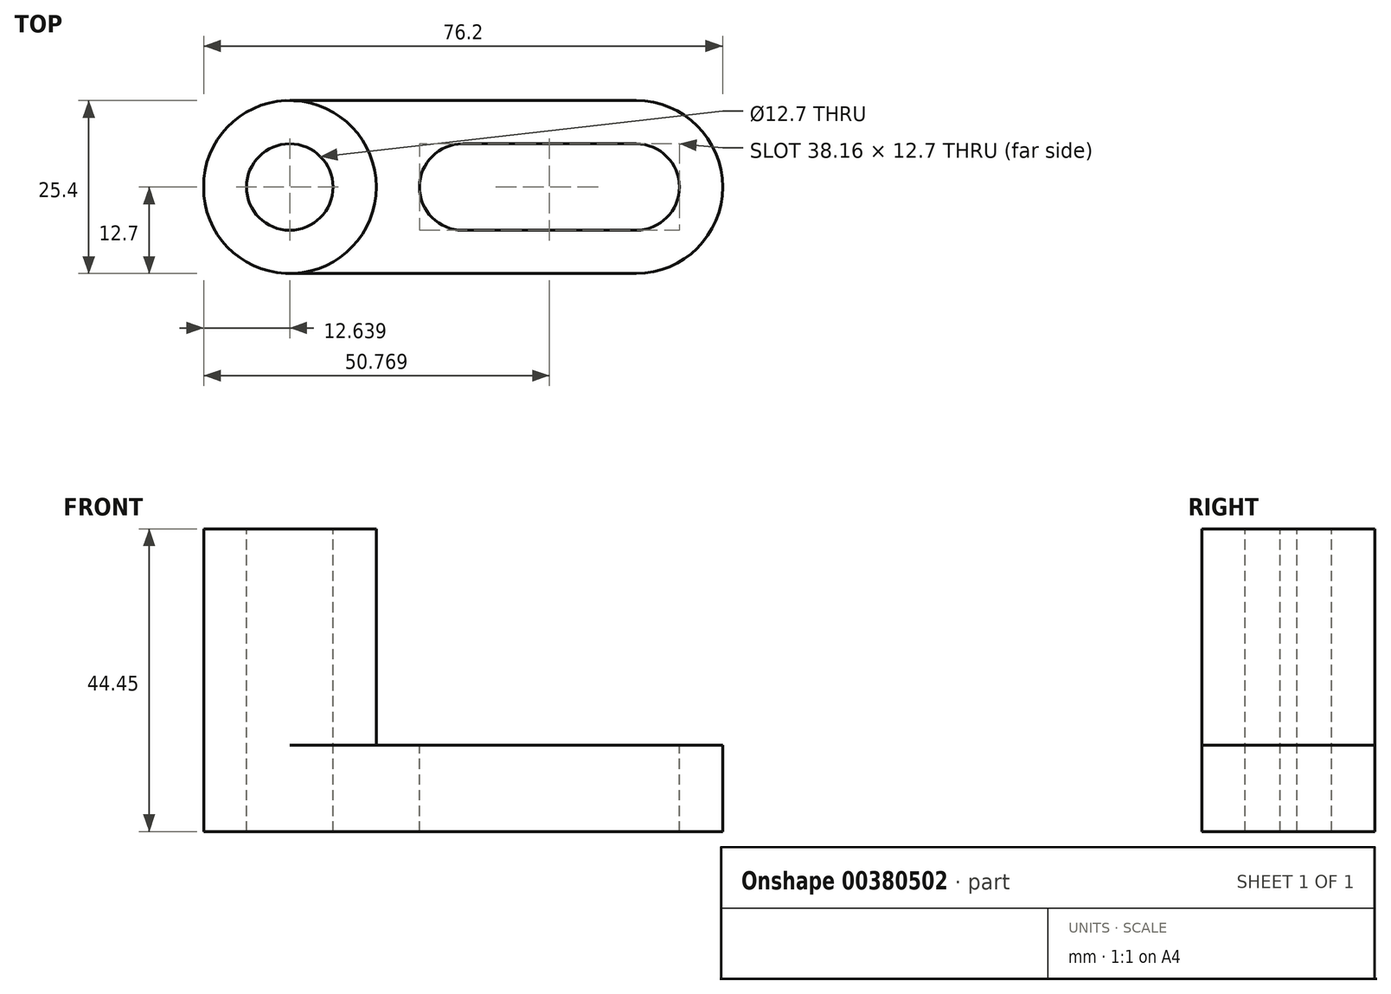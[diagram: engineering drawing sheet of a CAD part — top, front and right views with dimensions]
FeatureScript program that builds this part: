
annotation { "Feature Type Name" : "Feature", "Feature Type Description" : "" }
export const myFeature = defineFeature(function(context is Context, id is Id, definition is map)
    precondition{}
    {
        {
            var Q0;
            Q0=qCreatedBy(makeId("Front.planeOp"),FACE);
            var sketch = newSketch(context, id + "F0", { "sketchPlane" : qUnion([Q0])});
            skLineSegment(sketch, "E0", {"start": v(0, 0) * mm, "end": v(76.2, 0) * mm});
            skLineSegment(sketch, "E1", {"start": v(76.2, 0) * mm, "end": v(76.2, 12.7) * mm});
            skLineSegment(sketch, "E2", {"start": v(76.2, 12.7) * mm, "end": v(25.4, 12.7) * mm});
            skLineSegment(sketch, "E3", {"start": v(25.4, 12.7) * mm, "end": v(25.4, 44.45) * mm});
            skLineSegment(sketch, "E4", {"start": v(25.4, 44.45) * mm, "end": v(0, 44.45) * mm});
            skLineSegment(sketch, "E5", {"start": v(0, 44.45) * mm, "end": v(0, 0) * mm});
            skSolve(sketch);
        }
        {
            var Q0;
            Q0=makeQuery(id+"F0.imprint","IMPRINT",FACE,{"disambiguationData":[TD([[makeQuery(id+"F0.imprint","IMPRINT",EDGE,{"derivedFrom":sQuery(id+"F0.wireOp",EDGE,"E0")}),1.0]])]});
            extrude(context, id + "F1", {"entities" : qUnion([Q0]), "depth" : 25.4 * mm});
        }
        {
            var Q0;
            Q0=makeQuery(id+"F1.opExtrude","SWEPT_FACE",FACE,{"disambiguationData":[OSD([sQuery(id+"F0.wireOp",EDGE,"E4")])]});
            var sketch = newSketch(context, id + "F2", { "sketchPlane" : qUnion([Q0])});
            skCircle(sketch, "E6", {"center": v(12.64, -12.7) * mm, "radius": 12.7 * mm});
            skSolve(sketch);
        }
        {
            var Q0;
            {var subQ0=sQuery(id+"F2.wireOp",EDGE,"E6");var subQ1=sQuery(id+"F0.wireOp",EDGE,"E4");var subQ4=makeQuery(id+"F1.opExtrude","CAP_EDGE",EDGE,{"disambiguationData":[OSD([subQ1])],"isStart":false});var subQ5=makeQuery(id+"F2.imprint","INTERSECT",VERTEX,{"derivedFrom":[subQ4,subQ0]});Q0=makeQuery(id+"F2.imprint","IMPRINT",FACE,{"disambiguationData":[TD([[makeQuery(id+"F2.imprint","IMPRINT",EDGE,{"disambiguationData":[TD([[subQ5,1.0]])],"derivedFrom":subQ0}),-1.0]])]});}
            var Q1;
            {var subQ0=sQuery(id+"F2.wireOp",EDGE,"E6");var subQ1=sQuery(id+"F0.wireOp",EDGE,"E4");var subQ4=makeQuery(id+"F1.opExtrude","CAP_EDGE",EDGE,{"disambiguationData":[OSD([subQ1])],"isStart":true});var subQ5=makeQuery(id+"F2.imprint","INTERSECT",VERTEX,{"derivedFrom":[subQ4,subQ0]});Q1=makeQuery(id+"F2.imprint","IMPRINT",FACE,{"disambiguationData":[TD([[makeQuery(id+"F2.imprint","IMPRINT",EDGE,{"disambiguationData":[TD([[subQ5,-1.0]])],"derivedFrom":subQ0}),-1.0]])]});}
            var Q2;
            {var subQ1=sQuery(id+"F0.wireOp",EDGE,"E4");var subQ6=makeQuery(id+"F1.opExtrude","SWEPT_EDGE",EDGE,{"disambiguationData":[OSD([sQuery(id+"F0.wireOp",EDGE,"E3"),subQ1])]});Q2=makeQuery(id+"F2.imprint","IMPRINT",FACE,{"disambiguationData":[TD([[makeQuery(id+"F2.imprint","IMPRINT",EDGE,{"derivedFrom":subQ6}),1.0]])]});}
            extrude(context, id + "F3", {"entities" : qUnion([Q0, Q1, Q2]), "operationType" : NewBodyOperationType.REMOVE, "oppositeDirection" : true, "depth" : 31.75 * mm});
        }
        {
            var Q0;
            {var subQ0=sQuery(id+"F0.wireOp",EDGE,"E4");var subQ1=makeQuery(id+"F1.opExtrude","CAP_EDGE",EDGE,{"disambiguationData":[OSD([subQ0])],"isStart":false});var subQ2=sQuery(id+"F0.wireOp",EDGE,"E5");var subQ3=makeQuery(id+"F1.opExtrude","SWEPT_EDGE",EDGE,{"disambiguationData":[OSD([subQ0,subQ2])]});var subQ4=makeQuery(id+"F2.imprint","INTERSECT",VERTEX,{"derivedFrom":[subQ3,subQ1]});var subQ5=sQuery(id+"F2.wireOp",EDGE,"E6");var subQ6=makeQuery(id+"F2.imprint","INTERSECT",VERTEX,{"derivedFrom":[subQ1,subQ5]});Q0=makeQuery(id+"F3.boolean.opBoolean","COPY",FACE,{"derivedFrom":makeQuery(id+"F3.opExtrude","CAP_FACE",FACE,{"disambiguationData":[OSD([subQ0,subQ2,subQ5]),TDD([makeQuery(id+"F2.imprint","IMPRINT",EDGE,{"disambiguationData":[TD([[subQ6,1.0]])],"derivedFrom":subQ5}),makeQuery(id+"F2.imprint","IMPRINT",EDGE,{"disambiguationData":[TD([[subQ4,-1.0]])],"derivedFrom":subQ3}),makeQuery(id+"F2.imprint","IMPRINT",EDGE,{"disambiguationData":[TD([[subQ6,-1.0]])],"derivedFrom":subQ1})])],"isStart":false})});}
            var Q1;
            {var subQ0=sQuery(id+"F0.wireOp",EDGE,"E4");var subQ1=makeQuery(id+"F1.opExtrude","CAP_EDGE",EDGE,{"disambiguationData":[OSD([subQ0])],"isStart":true});var subQ2=sQuery(id+"F0.wireOp",EDGE,"E5");var subQ3=makeQuery(id+"F1.opExtrude","SWEPT_EDGE",EDGE,{"disambiguationData":[OSD([subQ0,subQ2])]});var subQ4=makeQuery(id+"F2.imprint","INTERSECT",VERTEX,{"derivedFrom":[subQ3,subQ1]});var subQ5=sQuery(id+"F2.wireOp",EDGE,"E6");var subQ6=makeQuery(id+"F2.imprint","INTERSECT",VERTEX,{"derivedFrom":[subQ1,subQ5]});Q1=makeQuery(id+"F3.boolean.opBoolean","COPY",FACE,{"derivedFrom":makeQuery(id+"F3.opExtrude","CAP_FACE",FACE,{"disambiguationData":[OSD([subQ0,subQ2,subQ5]),TDD([makeQuery(id+"F2.imprint","IMPRINT",EDGE,{"disambiguationData":[TD([[subQ6,-1.0]])],"derivedFrom":subQ5}),makeQuery(id+"F2.imprint","IMPRINT",EDGE,{"disambiguationData":[TD([[subQ4,1.0]])],"derivedFrom":subQ3}),makeQuery(id+"F2.imprint","IMPRINT",EDGE,{"disambiguationData":[TD([[subQ6,-1.0]])],"derivedFrom":subQ1})])],"isStart":false})});}
            extrude(context, id + "F4", {"entities" : qUnion([Q0, Q1]), "operationType" : NewBodyOperationType.REMOVE, "oppositeDirection" : true, "depth" : 12.7 * mm});
        }
        {
            var Q0;
            Q0=makeQuery(id+"F3.boolean.opBoolean","MERGE",FACE,{"derivedFrom":[makeQuery(id+"F1.opExtrude","SWEPT_FACE",FACE,{"disambiguationData":[OSD([sQuery(id+"F0.wireOp",EDGE,"E2")])]})],"fromTools":[makeQuery(id+"F3.opExtrude","CAP_FACE",FACE,{"disambiguationData":[OSD([sQuery(id+"F0.wireOp",EDGE,"E3"),sQuery(id+"F0.wireOp",EDGE,"E4"),sQuery(id+"F2.wireOp",EDGE,"E6")])],"isStart":false})]});
            var sketch = newSketch(context, id + "F5", { "sketchPlane" : qUnion([Q0])});
            skCircle(sketch, "E7", {"center": v(38.04, -12.7) * mm, "radius": 6.35 * mm});
            skCircle(sketch, "E8", {"center": v(63.5, -12.7) * mm, "radius": 6.35 * mm});
            skLineSegment(sketch, "E9", {"start": v(38.04, -6.35) * mm, "end": v(63.5, -6.35) * mm});
            skLineSegment(sketch, "E10", {"start": v(63.5, -19.05) * mm, "end": v(38.04, -19.05) * mm});
            skSolve(sketch);
        }
        {
            var Q0;
            {var subQ0=sQuery(id+"F5.wireOp",EDGE,"E8");var subQ1=makeQuery(id+"F5.imprint","INTERSECT",VERTEX,{"derivedFrom":[subQ0,sQuery(id+"F5.wireOp",EDGE,"E9")]});Q0=makeQuery(id+"F5.imprint","IMPRINT",FACE,{"disambiguationData":[TD([[makeQuery(id+"F5.imprint","IMPRINT",EDGE,{"disambiguationData":[TD([[subQ1,-1.0]])],"derivedFrom":subQ0}),1.0]])]});}
            var Q1;
            {var subQ0=sQuery(id+"F5.wireOp",EDGE,"E9");Q1=makeQuery(id+"F5.imprint","IMPRINT",FACE,{"disambiguationData":[TD([[makeQuery(id+"F5.imprint","IMPRINT",EDGE,{"derivedFrom":subQ0}),-1.0]])]});}
            var Q2;
            {var subQ0=sQuery(id+"F5.wireOp",EDGE,"E7");var subQ1=makeQuery(id+"F5.imprint","INTERSECT",VERTEX,{"derivedFrom":[subQ0,sQuery(id+"F5.wireOp",EDGE,"E9")]});Q2=makeQuery(id+"F5.imprint","IMPRINT",FACE,{"disambiguationData":[TD([[makeQuery(id+"F5.imprint","IMPRINT",EDGE,{"disambiguationData":[TD([[subQ1,-1.0]])],"derivedFrom":subQ0}),1.0]])]});}
            extrude(context, id + "F6", {"entities" : qUnion([Q0, Q1, Q2]), "operationType" : NewBodyOperationType.REMOVE, "oppositeDirection" : true, "depth" : 12.7 * mm});
        }
        {
            var Q0;
            Q0=makeQuery(id+"F3.boolean.opBoolean","MERGE",FACE,{"derivedFrom":[makeQuery(id+"F1.opExtrude","SWEPT_FACE",FACE,{"disambiguationData":[OSD([sQuery(id+"F0.wireOp",EDGE,"E2")])]})],"fromTools":[makeQuery(id+"F3.opExtrude","CAP_FACE",FACE,{"disambiguationData":[OSD([sQuery(id+"F0.wireOp",EDGE,"E3"),sQuery(id+"F0.wireOp",EDGE,"E4"),sQuery(id+"F2.wireOp",EDGE,"E6")])],"isStart":false})]});
            var sketch = newSketch(context, id + "F7", { "sketchPlane" : qUnion([Q0])});
            skArc(sketch, "E11", {"start": v(63.5, -25.4) * mm, "mid": v(76.2, -12.7) * mm, "end": v(63.5, 0) * mm});
            skSolve(sketch);
        }
        {
            var Q0;
            {var subQ0=sQuery(id+"F7.wireOp",EDGE,"E11");var subQ3=sQuery(id+"F0.wireOp",EDGE,"E2");var subQ6=makeQuery(id+"F1.opExtrude","SWEPT_EDGE",EDGE,{"disambiguationData":[OSD([sQuery(id+"F0.wireOp",EDGE,"E1"),subQ3])]});var subQ7=makeQuery(id+"F7.imprint","INTERSECT",VERTEX,{"derivedFrom":[subQ6,subQ0]});Q0=makeQuery(id+"F7.imprint","IMPRINT",FACE,{"disambiguationData":[TD([[makeQuery(id+"F7.imprint","IMPRINT",EDGE,{"disambiguationData":[TD([[subQ7,-1.0]])],"derivedFrom":subQ0}),-1.0]])]});}
            var Q1;
            {var subQ0=sQuery(id+"F7.wireOp",EDGE,"E11");var subQ3=sQuery(id+"F0.wireOp",EDGE,"E2");var subQ6=makeQuery(id+"F1.opExtrude","SWEPT_EDGE",EDGE,{"disambiguationData":[OSD([sQuery(id+"F0.wireOp",EDGE,"E1"),subQ3])]});var subQ7=makeQuery(id+"F7.imprint","INTERSECT",VERTEX,{"derivedFrom":[subQ6,subQ0]});Q1=makeQuery(id+"F7.imprint","IMPRINT",FACE,{"disambiguationData":[TD([[makeQuery(id+"F7.imprint","IMPRINT",EDGE,{"disambiguationData":[TD([[subQ7,1.0]])],"derivedFrom":subQ0}),-1.0]])]});}
            extrude(context, id + "F8", {"entities" : qUnion([Q0, Q1]), "operationType" : NewBodyOperationType.REMOVE, "oppositeDirection" : true, "depth" : 12.7 * mm});
        }
        {
            var Q0;
            Q0=makeQuery(id+"F1.opExtrude","SWEPT_FACE",FACE,{"disambiguationData":[OSD([sQuery(id+"F0.wireOp",EDGE,"E4")])]});
            var sketch = newSketch(context, id + "F9", { "sketchPlane" : qUnion([Q0])});
            skCircle(sketch, "E12", {"center": v(12.64, -12.7) * mm, "radius": 6.35 * mm});
            skSolve(sketch);
        }
        {
            var Q0;
            Q0=makeQuery(id+"F9.imprint","IMPRINT",FACE,{"disambiguationData":[TD([[makeQuery(id+"F9.imprint","IMPRINT",EDGE,{"derivedFrom":sQuery(id+"F9.wireOp",EDGE,"E12")}),1.0]])]});
            extrude(context, id + "F10", {"entities" : qUnion([Q0]), "operationType" : NewBodyOperationType.REMOVE, "oppositeDirection" : true, "depth" : 44.45 * mm});
        }
    });
